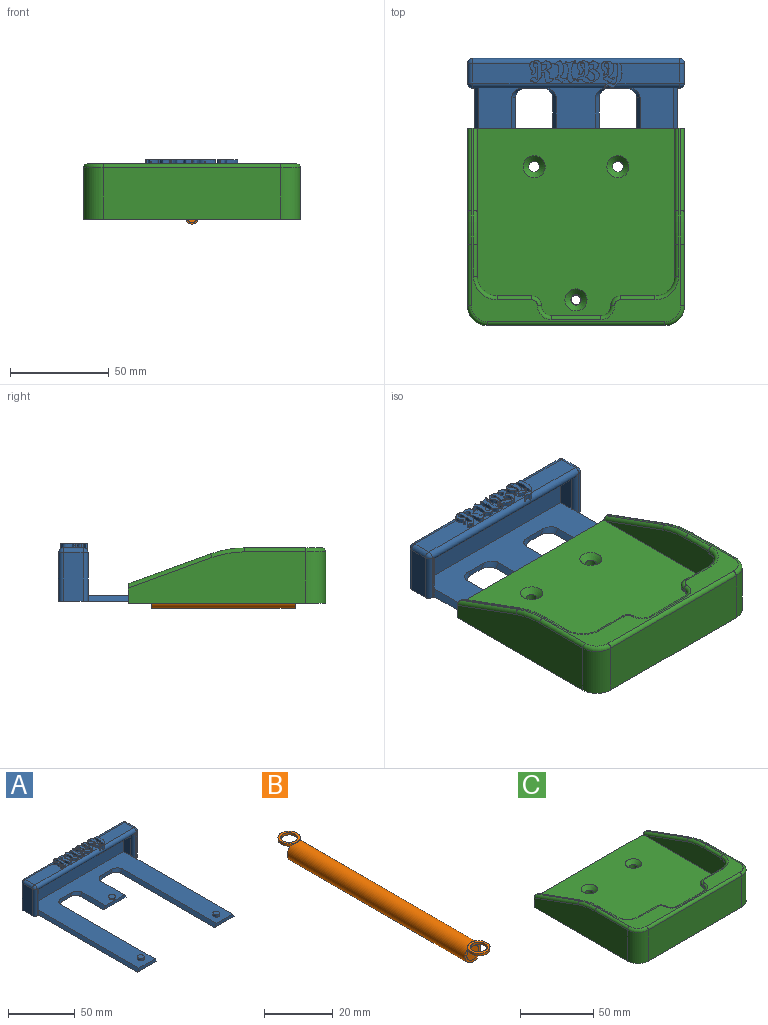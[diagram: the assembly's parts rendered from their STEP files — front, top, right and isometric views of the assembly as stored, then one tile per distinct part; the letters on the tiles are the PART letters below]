
ASSEMBLY  parts=3 mates=2
PART A: 76 faces, bbox 110x120x31.5 mm
  f0: plane 14.67x10.34mm, normal (0,0,1), area 67mm2, adj f1,f3,f39,f50,f63,f70,f73
  f1: cylinder r=2.5mm len=2.57mm, axis (-1,0,0), area 1mm2, adj f0,f73
  f2: plane 31.31x10.15mm, normal (0,0,1), area 296.1mm2, adj f39,f45,f50,f73
  f3: cylinder r=2.5mm len=1.83mm, axis (1,0,0), area 0.5mm2, adj f0,f70
  f4: plane 0.13x0.04mm, normal (0,0,1), area 0mm2, adj f39,f70
  f5: cylinder r=2.5mm len=1.84mm, axis (1,0,0), area 0.6mm2, adj f8,f63
  f6: plane 8.29x4.36mm, normal (0,0,1), area 20.2mm2, adj f39,f61
  f7: plane 33.42x10.69mm, normal (0,0,1), area 312.3mm2, adj f9,f39,f44,f50,f57
  f8: plane 27.37x10.3mm, normal (0,0,1), area 104.9mm2, adj f5,f39,f50,f57,f61,f63
  f9: cylinder r=2.5mm len=1.75mm, axis (1,0,0), area 0.5mm2, adj f7,f57
  f10: plane 24.5x0.5mm, normal (0,-1,0), area 12.3mm2, adj f30,f43,f49,f50
  f11: plane 19x7.5mm, normal (1,0,0), area 142.5mm2, adj f13,f14,f37,f49
  f12: plane 19x7.5mm, normal (-1,0,0), area 142.5mm2, adj f13,f14,f37,f51
  f13: plane 99x19mm, normal (0,-1,0), area 1881mm2, adj f11,f12,f14,f37
  f14: plane 115x99mm, normal (0,0,1), area 5135.6mm2, adj f11,f12,f13,f15,f16,f21,f22,f23
  f15: plane 20.46x3mm, normal (0,-1,0), area 56.2mm2, adj f14,f16,f29,f30
  f16: plane 107.5x3mm, normal (0.87,0,0.5), area 366.4mm2, adj f14,f15,f30,f51
  f17: plane 24.5x0.5mm, normal (0,-1,0), area 12.3mm2, adj f30,f46,f50,f51
  f18: plane 24.5x10mm, normal (1,0,0), area 245mm2, adj f30,f40,f45,f46
  f19: plane 105x24.5mm, normal (0,1,0), area 2572.5mm2, adj f30,f38,f39,f40
  f20: plane 24.5x10mm, normal (-1,0,0), area 245mm2, adj f30,f38,f43,f44
  f21: plane 107.5x3mm, normal (-0.87,0,0.5), area 366.4mm2, adj f14,f22,f30,f49
  f22: plane 20.46x3mm, normal (0,-1,0), area 56.2mm2, adj f14,f21,f23,f30
  f23: plane 100x3mm, normal (0.87,0,0.5), area 346.4mm2, adj f14,f22,f30,f53
  f24: plane 10.95x3mm, normal (0,-1,0), area 27.7mm2, adj f14,f30,f53,f54
  f25: plane 25x3mm, normal (-0.87,0,0.5), area 86.6mm2, adj f14,f26,f30,f54
  f26: plane 23.46x3mm, normal (0,-1,0), area 65.2mm2, adj f14,f25,f27,f30
  f27: plane 25x3mm, normal (0.87,0,0.5), area 86.6mm2, adj f14,f26,f30,f55
  f28: plane 10.95x3mm, normal (0,-1,0), area 27.7mm2, adj f14,f30,f52,f55
  f29: plane 100x3mm, normal (-0.87,0,0.5), area 346.4mm2, adj f14,f15,f30,f52
  f30: plane 120x110mm, normal (0,0,-1), area 6670.7mm2, adj f10,f15,f16,f17,f18,f19,f20,f21
  f31: plane 5x5mm, normal (0,0,1), area 19.6mm2, adj f32
  f32: cylinder r=2.5mm len=5mm, axis (0,0,-1), area 31.4mm2, adj f14,f31
  f33: plane 5x5mm, normal (0,0,1), area 19.6mm2, adj f34
  f34: cylinder r=2.5mm len=5mm, axis (0,0,-1), area 31.4mm2, adj f14,f33
  f35: plane 5x5mm, normal (0,0,1), area 19.6mm2, adj f36
  f36: cone r=2.5mm half-angle=20deg, axis (0,0,1), area 28.6mm2, adj f14,f35
  f37: plane 99x7.5mm, normal (0,0,-1), area 742.5mm2, adj f11,f12,f13,f50
  f38: cylinder r=2.5mm len=24.5mm, axis (0,0,-1), area 96.2mm2, adj f19,f20,f30,f41
  f39: cylinder r=2.5mm len=105mm, axis (1,0,0), area 386.3mm2, adj f0,f2,f4,f6,f7,f8,f19,f41
  f40: cylinder r=2.5mm len=24.5mm, axis (0,0,-1), area 96.2mm2, adj f18,f19,f30,f42
  f41: sphere r=2.5mm, area 9.8mm2, adj f38,f39,f44
  f42: sphere r=2.5mm, area 9.8mm2, adj f39,f40,f45
  f43: cylinder r=2.5mm len=24.5mm, axis (0,0,1), area 96.2mm2, adj f10,f20,f30,f47
  f44: cylinder r=2.5mm len=10mm, axis (0,1,0), area 39.3mm2, adj f7,f20,f41,f47
  f45: cylinder r=2.5mm len=10mm, axis (0,-1,0), area 39.3mm2, adj f2,f18,f42,f48
  f46: cylinder r=2.5mm len=24.5mm, axis (0,0,1), area 96.2mm2, adj f17,f18,f30,f48
  f47: sphere r=2.5mm, area 9.8mm2, adj f43,f44,f50
  f48: sphere r=2.5mm, area 9.8mm2, adj f45,f46,f50
  f49: cylinder r=2.5mm len=24.5mm, axis (0,0,-1), area 83.8mm2, adj f10,f11,f21,f30,f50
  f50: cylinder r=2.5mm len=105mm, axis (-1,0,0), area 796.8mm2, adj f0,f2,f7,f8,f10,f17,f37,f47
  f51: cylinder r=2.5mm len=24.5mm, axis (0,0,1), area 83.8mm2, adj f12,f16,f17,f30,f50
  f52: cylinder r=5mm len=8mm, axis (-0.5,0,-0.87), area 27.2mm2, adj f14,f28,f29,f30
  f53: cylinder r=5mm len=8mm, axis (0.5,0,-0.87), area 27.2mm2, adj f14,f23,f24,f30
  f54: cylinder r=5mm len=8mm, axis (-0.5,0,-0.87), area 27.2mm2, adj f14,f24,f25,f30
  f55: cylinder r=5mm len=8mm, axis (0.5,0,-0.87), area 27.2mm2, adj f14,f27,f28,f30
  f56: plane 2x0.57mm, normal (0,-1,0), area 1.1mm2, adj f50,f57,f59
  f57: extruded ~11.62x11.24mm, area 159.7mm2, adj f7,f8,f9,f39,f56,f59
  f58: extruded ~3.43x2.85mm, area 20.5mm2, adj f59,f60
  f59: plane 12.41x12.02mm, normal (0,0,1), area 69.5mm2, adj f56,f57,f58
  f60: plane 3.61x3.13mm, normal (0,0,1), area 7.6mm2, adj f58
  f61: extruded ~10.89x10.48mm, area 132.5mm2, adj f6,f8,f39,f62
  f62: plane 11.49x11.02mm, normal (0,0,1), area 53mm2, adj f61
  f63: extruded ~11.32x11.23mm, area 128.1mm2, adj f0,f5,f8,f39,f65,f67
  f64: extruded ~3.13x2.61mm, area 19.1mm2, adj f67,f69
  f65: plane 2x0.16mm, normal (0,-1,0), area 0.3mm2, adj f50,f63,f67
  f66: extruded ~4.84x4.52mm, area 28.8mm2, adj f67,f68
  f67: plane 11.71x11.51mm, normal (0,0,1), area 68.6mm2, adj f63,f64,f65,f66
  f68: plane 4.96x4.76mm, normal (0,0,1), area 13.6mm2, adj f66
  f69: plane 3.24x2.71mm, normal (0,0,1), area 6.3mm2, adj f64
  f70: extruded ~10.82x6.66mm, area 105.1mm2, adj f0,f3,f4,f39,f71,f72
  f71: plane 2x0.97mm, normal (0,1,0), area 1.9mm2, adj f39,f70,f72
  f72: plane 11.09x7.18mm, normal (0,0,1), area 37mm2, adj f70,f71
  f73: extruded ~12.38x8.96mm, area 78.5mm2, adj f0,f1,f2,f50,f74,f75
  f74: plane 2x2mm, normal (0,1,0), area 4mm2, adj f39,f73,f75
  f75: plane 12.76x9.26mm, normal (0,0,1), area 29.4mm2, adj f73,f74
PART B: 13 faces, bbox 6.5x84.4x6.5 mm
  f0: plane 6.5x5.7mm, normal (0,1,0), area 30.8mm2, adj f1,f12
  f1: cylinder r=3.25mm len=73mm, axis (0,1,0), area 1485.8mm2, adj f0,f2,f8,f9
  f2: plane 6.5x5.7mm, normal (0,-1,0), area 12mm2, adj f1,f3,f6
  f3: plane 6.5x5.7mm, normal (0,0,1), area 12mm2, adj f2,f4,f8
  f4: cylinder r=2.45mm len=4.9mm, axis (0,0,-1), area 12.3mm2, adj f3,f5
  f5: plane 6.5x6.5mm, normal (0,0,-1), area 14.3mm2, adj f4,f8
  f6: cylinder r=2.45mm len=73mm, axis (0,1,0), area 1123.7mm2, adj f2,f7
  f7: plane 4.9x4.9mm, normal (0,-1,0), area 18.9mm2, adj f6
  f8: cylinder r=3.25mm len=6.5mm, axis (0,0,-1), area 13.9mm2, adj f1,f3,f5
  f9: cylinder r=3.25mm len=6.5mm, axis (0,0,-1), area 13.9mm2, adj f1,f10,f12
  f10: plane 6.5x6.5mm, normal (0,0,-1), area 14.3mm2, adj f9,f11
  f11: cylinder r=2.45mm len=4.9mm, axis (0,0,-1), area 12.3mm2, adj f10,f12
  f12: plane 6.5x5.7mm, normal (0,0,1), area 12mm2, adj f0,f9,f11
PART C: 88 faces, bbox 111.7x101.5x28.8 mm
  f0: plane 37.5x20mm, normal (0,0,-1), area 346.5mm2, adj f1,f2,f4,f45,f47,f49
  f1: plane 17.5x1mm, normal (0,1,0), area 17.5mm2, adj f0,f47,f49,f69
  f2: plane 94.1x18mm, normal (-1,0,0), area 1224.6mm2, adj f0,f4,f38,f49,f65,f66,f67
  f3: plane 94.1x18mm, normal (1,0,0), area 1224.6mm2, adj f4,f38,f42,f48,f77,f78,f79
  f4: plane 100x18mm, normal (0,1,0), area 1725mm2, adj f0,f2,f3,f38,f42,f44,f45,f72
  f5: plane 65x2mm, normal (-1,0,0), area 130mm2, adj f9,f10,f37,f40
  f6: plane 2x1mm, normal (0,1,0), area 2mm2, adj f10,f11,f37,f40
  f7: plane 65x2mm, normal (1,0,0), area 130mm2, adj f11,f12,f37,f40
  f8: plane 2x1mm, normal (0,-1,0), area 2mm2, adj f9,f12,f37,f40
  f9: cylinder r=2.5mm len=2.5mm, axis (0,0,-1), area 7.9mm2, adj f5,f8,f37,f40
  f10: cylinder r=2.5mm len=2.5mm, axis (0,0,-1), area 7.9mm2, adj f5,f6,f37,f40
  f11: cylinder r=2.5mm len=2.5mm, axis (0,0,-1), area 7.9mm2, adj f6,f7,f37,f40
  f12: cylinder r=2.5mm len=2.5mm, axis (0,0,-1), area 7.9mm2, adj f7,f8,f37,f40
  f13: plane 65x2mm, normal (1,0,0), area 130mm2, adj f17,f18,f36,f39
  f14: plane 2x1mm, normal (0,-1,0), area 2mm2, adj f18,f19,f36,f39
  f15: plane 65x2mm, normal (-1,0,0), area 130mm2, adj f19,f20,f36,f39
  f16: plane 2x1mm, normal (0,1,0), area 2mm2, adj f17,f20,f36,f39
  f17: cylinder r=2.5mm len=2.5mm, axis (0,0,-1), area 7.9mm2, adj f13,f16,f36,f39
  f18: cylinder r=2.5mm len=2.5mm, axis (0,0,-1), area 7.9mm2, adj f13,f14,f36,f39
  f19: cylinder r=2.5mm len=2.5mm, axis (0,0,-1), area 7.9mm2, adj f14,f15,f36,f39
  f20: cylinder r=2.5mm len=2.5mm, axis (0,0,-1), area 7.9mm2, adj f15,f16,f36,f39
  f21: plane 22.5x4mm, normal (0,1,0), area 80.8mm2, adj f22,f34,f37,f81
  f22: plane 85x4mm, normal (0.87,0,-0.5), area 392.6mm2, adj f21,f28,f34,f37
  f23: plane 85x4mm, normal (-0.87,0,-0.5), area 392.6mm2, adj f24,f28,f34,f35
  f24: plane 5.27x4mm, normal (0,1,0), area 16.5mm2, adj f23,f25,f34,f35
  f25: cylinder r=7.5mm len=15mm, axis (0,0,-1), area 110.4mm2, adj f24,f26,f34,f35
  f26: plane 5.27x4mm, normal (0,1,0), area 16.5mm2, adj f25,f27,f34,f35
  f27: plane 85x4mm, normal (0.87,0,-0.5), area 392.6mm2, adj f26,f28,f34,f35
  f28: plane 110x9.8mm, normal (0,1,0), area 642.1mm2, adj f22,f23,f27,f29,f31,f33,f34,f35
  f29: plane 85x4mm, normal (-0.87,0,-0.5), area 392.6mm2, adj f28,f30,f34,f36
  f30: plane 22.5x4mm, normal (0,1,0), area 80.8mm2, adj f29,f34,f36,f80
  f31: plane 90x26mm, normal (-1,0,0), area 1874.5mm2, adj f28,f34,f51,f56,f57,f58
  f32: plane 90x26mm, normal (0,-1,0), area 2340mm2, adj f34,f50,f51,f60
  f33: plane 90x26mm, normal (1,0,0), area 1874.5mm2, adj f28,f34,f50,f62,f63,f64
  f34: plane 110x100mm, normal (0,0,-1), area 4841.6mm2, adj f21,f22,f23,f24,f25,f26,f27,f28
  f35: plane 94.5x20.38mm, normal (0,0,-1), area 1826.6mm2, adj f23,f24,f25,f26,f27,f28,f82
  f36: plane 85x17.88mm, normal (0,0,-1), area 1105.3mm2, adj f13,f14,f15,f16,f17,f18,f19,f20
  f37: plane 85x17.88mm, normal (0,0,-1), area 1105.3mm2, adj f5,f6,f7,f8,f9,f10,f11,f12
  f38: plane 100.05x95mm, normal (0,0,1), area 9204.5mm2, adj f2,f3,f4,f28,f65,f79,f83,f85
  f39: plane 70x6mm, normal (0,0,-1), area 414.6mm2, adj f13,f14,f15,f16,f17,f18,f19,f20
  f40: plane 70x6mm, normal (0,0,-1), area 414.6mm2, adj f5,f6,f7,f8,f9,f10,f11,f12
  f41: plane 106x39.18mm, normal (0,0,1), area 883.9mm2, adj f54,f55,f58,f59,f60,f61,f62,f67
  f42: plane 37.5x20mm, normal (0,0,-1), area 346.5mm2, adj f3,f4,f43,f44,f46,f48
  f43: plane 17.5x1mm, normal (0,1,0), area 17.5mm2, adj f42,f46,f48,f75
  f44: cylinder r=5mm len=5mm, axis (0,0,1), area 7.9mm2, adj f4,f42,f46,f73
  f45: cylinder r=5mm len=5mm, axis (0,0,1), area 7.9mm2, adj f0,f4,f47,f71
  f46: cylinder r=5mm len=5mm, axis (0,0,1), area 7.9mm2, adj f42,f43,f44,f74
  f47: cylinder r=5mm len=5mm, axis (0,0,1), area 7.9mm2, adj f0,f1,f45,f70
  f48: cylinder r=10mm len=10mm, axis (0,0,-1), area 15.7mm2, adj f3,f42,f43,f76
  f49: cylinder r=10mm len=10mm, axis (0,0,1), area 15.7mm2, adj f0,f1,f2,f68
  f50: cylinder r=10mm len=26mm, axis (0,0,-1), area 408.4mm2, adj f32,f33,f34,f61
  f51: cylinder r=10mm len=26mm, axis (0,0,1), area 408.4mm2, adj f31,f32,f34,f59
  f52: plane 41.72x15.18mm, normal (0,0.34,0.94), area 44.4mm2, adj f28,f54,f56,f79
  f53: plane 41.72x15.18mm, normal (0,0.34,0.94), area 44.4mm2, adj f28,f55,f64,f65
  f54: cylinder r=50mm len=17.1mm, axis (-1,0,0), area 17.5mm2, adj f41,f52,f57,f78
  f55: cylinder r=50mm len=17.1mm, axis (-1,0,0), area 17.5mm2, adj f41,f53,f63,f66
  f56: cylinder r=2mm len=43.08mm, axis (0,0.94,-0.34), area 140.3mm2, adj f28,f31,f52,f57
  f57: torus R=48mm, axis (-1,0,0), area 54mm2, adj f31,f54,f56,f58
  f58: cylinder r=2mm len=31.18mm, axis (0,1,0), area 98mm2, adj f31,f41,f57,f59
  f59: torus R=8mm, axis (0,0,1), area 45.8mm2, adj f41,f51,f58,f60
  f60: cylinder r=2mm len=90mm, axis (1,0,0), area 282.7mm2, adj f32,f41,f59,f61
  f61: torus R=8mm, axis (0,0,1), area 45.8mm2, adj f41,f50,f60,f62
  f62: cylinder r=2mm len=31.18mm, axis (0,-1,0), area 98mm2, adj f33,f41,f61,f63
  f63: torus R=48mm, axis (-1,0,0), area 54mm2, adj f33,f55,f62,f64
  f64: cylinder r=2mm len=43.08mm, axis (0,0.94,-0.34), area 140.3mm2, adj f28,f33,f53,f63
  f65: cylinder r=2mm len=42.98mm, axis (0,0.94,-0.34), area 140.1mm2, adj f2,f28,f38,f53,f66
  f66: torus R=48mm, axis (-1,0,0), area 54mm2, adj f2,f55,f65,f67
  f67: cylinder r=2mm len=16.18mm, axis (0,1,0), area 50.8mm2, adj f2,f41,f66,f68
  f68: torus R=12mm, axis (0,0,1), area 52.9mm2, adj f41,f49,f67,f69
  f69: cylinder r=2mm len=17.5mm, axis (1,0,0), area 55mm2, adj f1,f41,f68,f70
  f70: torus R=3mm, axis (0,0,1), area 21.1mm2, adj f41,f47,f69,f71
  f71: torus R=7mm, axis (0,0,1), area 28.3mm2, adj f41,f45,f70,f72
  f72: cylinder r=2mm len=25mm, axis (1,0,0), area 78.5mm2, adj f4,f41,f71,f73
  f73: torus R=7mm, axis (0,0,1), area 28.3mm2, adj f41,f44,f72,f74
  f74: torus R=3mm, axis (0,0,1), area 21.1mm2, adj f41,f46,f73,f75
  f75: cylinder r=2mm len=17.5mm, axis (1,0,0), area 55mm2, adj f41,f43,f74,f76
  f76: torus R=12mm, axis (0,0,1), area 52.9mm2, adj f41,f48,f75,f77
  f77: cylinder r=2mm len=16.18mm, axis (0,-1,0), area 50.8mm2, adj f3,f41,f76,f78
  f78: torus R=48mm, axis (-1,0,0), area 54mm2, adj f3,f54,f77,f79
  f79: cylinder r=2mm len=42.98mm, axis (0,0.94,-0.34), area 140.1mm2, adj f3,f28,f38,f52,f78
  f80: plane 85x4mm, normal (0.87,0,-0.5), area 392.6mm2, adj f28,f30,f34,f36
  f81: plane 85x4mm, normal (-0.87,0,-0.5), area 392.6mm2, adj f21,f28,f34,f37
  f82: cylinder r=2.75mm len=5.5mm, axis (0,0,1), area 19.9mm2, adj f35,f83
  f83: cone r=2.75mm half-angle=45deg, axis (0,0,1), area 105.7mm2, adj f38,f82
  f84: cylinder r=2.75mm len=5.5mm, axis (0,0,1), area 89mm2, adj f34,f85
  f85: cone r=2.75mm half-angle=45deg, axis (0,0,1), area 105.7mm2, adj f38,f84
  f86: cylinder r=2.75mm len=5.5mm, axis (0,0,1), area 89mm2, adj f34,f87
  f87: cone r=2.75mm half-angle=45deg, axis (0,0,1), area 105.7mm2, adj f38,f86
PLACE A rot(axis=(0,0,1),0deg) t=(-46.43,-114.73,-40.85)mm
PLACE B t=(-46.43,-58.8,-40.1)mm
PLACE C t=(-46.43,-30.2,-40.85)mm
MATE fastened B.f9 <-> C.f82  axis (0,0,-1) through (-46.43,-97.75,-36.85)mm
MATE pin_slot A.f34 <-> C.f40  axis (0,0,1) through (-6.43,-87.78,-34.85)mm
